# Revit family: DC_Rheem_PLM_HeavyDutyGas_631275
name_source: partatom
category: Mechanical Equipment
revit_build: Autodesk Revit 2018 (Build: 20170223_1515(x64)
units: mm (PartAtom-declared; Revit-internal decimal feet)

## family parameters
Cut with Voids When Loaded = No
Host = Face
Part Type = Normal
Room Calculation Point = No
Round Connector Dimension = Use Radius
Shared = No

## types (2) — shared parameters
ColdWaterInletPipeDiameter_ANZRS = 32 mm  [stored 0.104987 ft]
ColdWaterInletPipeRadius_ANZRS = 16 mm  [stored 0.0524934 ft]
CylinderDiameterD2_ANZRS = 643 mm  [stored 2.10958 ft]
CylinderRadius_ANZRS = 322 mm
Description = Heavy Duty Gas Storage - Outdoor - 275L - 200 MJ/h - Natural gas
GasInletPipeRadius_ANZRS = 10 mm  [stored 0.0328084 ft]
HotWaterOutletPipeDiameter_ANZRS = 32 mm  [stored 0.104987 ft]
HotWaterOutletPipeRadius_ANZRS = 16 mm  [stored 0.0524934 ft]
Manufacturer = Rheem
Materials_ANZRS = Rheem - Joey Grey Steel
T&PRValveRadius_ANZRS = 16 mm  [stored 0.0524934 ft]
Thicknesss_ANZRS = 35 mm
TopDiameterD1_ANZRS = 189 mm
Type Comments = 1000L first hour delivery @ 50oC rise - Suitable for indoor installation with a room sealed kit
URL = http://www.rheem.com.au
zero-valued in all types: Default Elevation

## per-type parameters (varying)
| type | Model |
| Heavy Duty Gas Storage - Outdoor - 275L - 200 MJ/h - Natural gas | 631275N0 |
| Heavy Duty Gas Storage - Outdoor - 275L - 190 MJ/h - Propane gas | 631275P0 |

note: [stored X ft] marks values corroborated as IEEE doubles in the binary element streams (Revit-internal decimal feet)

## geometry (parser evidence)
native form markers: Blend x6, Sweep x5
no freeform markers — native parametric forms only
